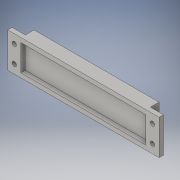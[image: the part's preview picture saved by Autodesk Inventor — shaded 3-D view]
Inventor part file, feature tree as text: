
AUTODESK INVENTOR PART (.ipt)
format: ipt  version: 2016 (Build 200138000, 138)  size: 163,840 bytes
history: native  units: in
note: dims shown in document units (in); Inventor stores cm internally (conversion verified against a paired STEP export)
features: sketch x6, extrude x3, hole x3
ambient origin geometry x8: Origin, YZ Plane, XZ Plane, XY Plane, X Axis, Y Axis, Z Axis, Center Point
bodies: Solid1 (feature_tree)
feature tree (12):
  extrude  "Extrusion1"  Depth=0.75in
  hole  "Hole1"  [1 undecoded]
  extrude  "Extrusion2"  TaperAngle=0.0deg  [1 undecoded]
  extrude  "Extrusion3"  Depth=0.5in
  hole  "Hole2"  [1 undecoded]
  hole  "Hole3"  [1 undecoded]
  sketch  "Sketch1"  dims[d0=8.65in d1=0.75in]
  sketch  "Sketch2"  dims[d2=2.0in d3=0.0in d4=0.0in]
  sketch  "Sketch3"  dims[d5=0.0in d6=0.0in]
  sketch  "Sketch6"  dims[d7=0.0in d8=0.5in]
  sketch  "Sketch7"  dims[d9=0.5in d10=0.375in]
  sketch  "Sketch8"  dims[d11=0.375in d12=0.25in d13=0.75in d14=0.375in d15=0.25in d16=0.5635in d17=1.0in d18=0.8108in d19=0.75in d20=0.75in d21=0.25in d22=0.25in d23=0.25in d24=0.0in d25=0.0in d26=0.5in d27=0.0in d28=0.75in d32=0.75in d33=0.0in d34=0.25in d35=3.0in d36=0.0in d37=2.0in d38=0.375in d39=2.0in d40=0.375in d41=0.1935in d42=0.75in d43=0.375in d44=0.25in d45=0.5635in d46=1.0in d47=0.8108in d48=4.5in d49=0.375in d50=0.1935in d51=0.75in d52=0.375in d53=0.25in d54=0.5635in d55=1.0in d56=0.8108in]
note: 4 required parameter values undecoded (feature->parameter linkage not recoverable at this tier; creation-order binding heuristic only, values carry confidence <= 0.55)
